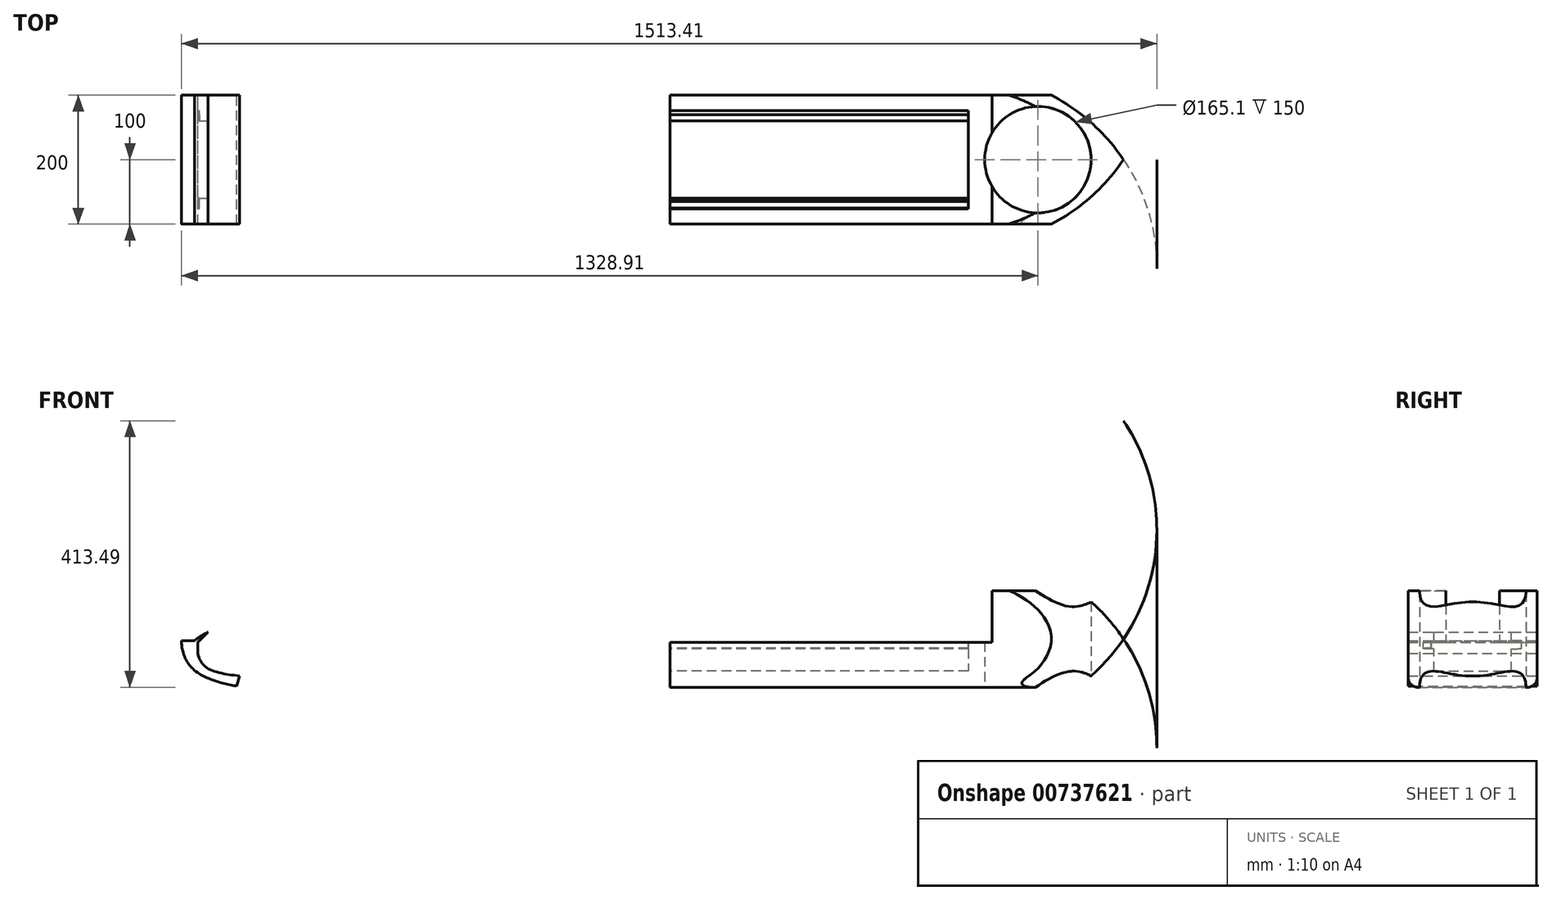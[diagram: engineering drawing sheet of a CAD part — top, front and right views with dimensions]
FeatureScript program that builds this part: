
annotation { "Feature Type Name" : "Feature", "Feature Type Description" : "" }
export const myFeature = defineFeature(function(context is Context, id is Id, definition is map)
    precondition{}
    {
        {
            var Q0;
            Q0=qCreatedBy(makeId("Front.planeOp"),FACE);
            var sketch = newSketch(context, id + "F0", { "sketchPlane" : qUnion([Q0])});
            skLineSegment(sketch, "E0", {"start": v(-811.66, 0) * mm, "end": v(235.58, 0) * mm});
            skPoint(sketch, "E1.visualSharp", {"position": v(572.1, 0) * mm});
            skArc(sketch, "E2", {"start": v(-800.68, 138.75) * mm, "mid": v(-782.15, 142.68) * mm, "end": v(-763.5, 145.97) * mm});
            skArc(sketch, "E3", {"start": v(-763.5, 145.97) * mm, "mid": v(-264.12, 186.3) * mm, "end": v(235.58, 150) * mm});
            skLineSegment(sketch, "E4", {"start": v(235.58, 150) * mm, "end": v(235.58, 0) * mm});
            skLineSegment(sketch, "E5", {"start": v(0, 0) * mm, "end": v(306.95, 0) * mm});
            skPoint(sketch, "E6.orphan", {"position": v(-1022, 0) * mm});
            skLineSegment(sketch, "E7", {"start": v(-918.7, 0) * mm, "end": v(-918.7, 40) * mm});
            skLineSegment(sketch, "E8", {"start": v(-264.12, 186.3) * mm, "end": v(-264.12, 0) * mm});
            skPoint(sketch, "E8.endSnap0", {"position": v(-288.04, 0) * mm});
            skLineSegment(sketch, "E9", {"start": v(-1074.98, 0) * mm, "end": v(-1074.98, 186.3) * mm});
            skLineSegment(sketch, "E10", {"start": v(-1074.98, 186.3) * mm, "end": v(-1074.98, 161.3) * mm});
            skLineSegment(sketch, "E11", {"start": v(-997, 0) * mm, "end": v(-997, 70) * mm});
            skLineSegment(sketch, "E12", {"start": v(-997, 70) * mm, "end": v(235.58, 70) * mm});
            skFitSpline(sketch, "E13", {"points": [v(-1001.83, 72.5) * mm, v(-931.39, 96.18) * mm, v(-756.37, 114.5) * mm, v(-264.12, 141) * mm, v(235.58, 119.1) * mm, v(272.81, 113.33) * mm], "startDerivative": vector(592.82, 474.11) * mm, "endDerivative": vector(301.15, -59.77) * mm});
            skLineSegment(sketch, "E14", {"start": v(-264.12, 70) * mm, "end": v(-264.12, 141) * mm});
            skCircle(sketch, "E15", {"center": v(-946.75, 72.5) * mm, "radius": 2.5 * mm});
            skLineSegment(sketch, "E16.bottom", {"start": v(-862, 70) * mm, "end": v(-851, 70) * mm});
            skLineSegment(sketch, "E16.top", {"start": v(-862, 81) * mm, "end": v(-851, 81) * mm});
            skLineSegment(sketch, "E16.left", {"start": v(-862, 70) * mm, "end": v(-862, 81) * mm});
            skLineSegment(sketch, "E16.right", {"start": v(-851, 70) * mm, "end": v(-851, 81) * mm});
            skLineSegment(sketch, "E17.bottom", {"start": v(-748, 70) * mm, "end": v(-741, 70) * mm});
            skLineSegment(sketch, "E17.top", {"start": v(-748, 77) * mm, "end": v(-741, 77) * mm});
            skLineSegment(sketch, "E17.left", {"start": v(-748, 70) * mm, "end": v(-748, 77) * mm});
            skLineSegment(sketch, "E17.right", {"start": v(-741, 70) * mm, "end": v(-741, 77) * mm});
            skCircle(sketch, "E18", {"center": v(-32.75, 73.75) * mm, "radius": 2.5 * mm});
            skLineSegment(sketch, "E19.bottom", {"start": v(0, 70) * mm, "end": v(7, 70) * mm});
            skLineSegment(sketch, "E19.top", {"start": v(0, 77) * mm, "end": v(7, 77) * mm});
            skLineSegment(sketch, "E19.left", {"start": v(0, 70) * mm, "end": v(0, 77) * mm});
            skLineSegment(sketch, "E19.right", {"start": v(7, 70) * mm, "end": v(7, 77) * mm});
            skLineSegment(sketch, "E20.bottom", {"start": v(136, 70) * mm, "end": v(143, 70) * mm});
            skLineSegment(sketch, "E20.top", {"start": v(136, 77) * mm, "end": v(143, 77) * mm});
            skLineSegment(sketch, "E20.left", {"start": v(136, 70) * mm, "end": v(136, 77) * mm});
            skLineSegment(sketch, "E20.right", {"start": v(143, 70) * mm, "end": v(143, 77) * mm});
            skLineSegment(sketch, "E21", {"start": v(-1001.83, 72.5) * mm, "end": v(-997, 70) * mm});
            skFitSpline(sketch, "E22", {"points": [v(-800.68, 138.75) * mm, v(-939.96, 114.34) * mm, v(-993, 98.83) * mm, v(-1017.8, 82.36) * mm, v(-1021.91, 72.5) * mm, v(-1001.83, 26.4) * mm, v(-918.7, 0) * mm], "startDerivative": vector(-432.5, -65.01) * mm, "endDerivative": vector(192.07, 0) * mm});
            skLineSegment(sketch, "E23", {"start": v(-918.7, 0) * mm, "end": v(-811.66, 0) * mm});
            skLineSegment(sketch, "E24", {"start": v(-997, 70) * mm, "end": v(-980.83, 85.6) * mm});
            skLineSegment(sketch, "E25.bottom", {"start": v(-423, 70) * mm, "end": v(-471, 70) * mm});
            skLineSegment(sketch, "E25.top", {"start": v(-423, 97.8) * mm, "end": v(-471, 97.8) * mm});
            skLineSegment(sketch, "E25.left", {"start": v(-423, 70) * mm, "end": v(-423, 97.8) * mm});
            skLineSegment(sketch, "E25.right", {"start": v(-471, 70) * mm, "end": v(-471, 97.8) * mm});
            skArc(sketch, "E26", {"start": v(-423, 97.8) * mm, "mid": v(-447, 121.8) * mm, "end": v(-471, 97.8) * mm});
            skLineSegment(sketch, "E27", {"start": v(-1001.83, 72.5) * mm, "end": v(-997, 72.5) * mm});
            skLineSegment(sketch, "E28", {"start": v(-980.83, 85.6) * mm, "end": v(-997, 72.5) * mm});
            skLineSegment(sketch, "E29", {"start": v(-997, 70) * mm, "end": v(-997, 72.5) * mm});
            skLineSegment(sketch, "E30", {"start": v(-997, 72.5) * mm, "end": v(-997.16, 76.05) * mm});
            skLineSegment(sketch, "E31", {"start": v(-936.1, 1.72) * mm, "end": v(-932.14, 17.49) * mm});
            skFitSpline(sketch, "E32", {"points": [v(-932.14, 17.49) * mm, v(-987.1, 33.77) * mm, v(-1001.83, 72.5) * mm], "startDerivative": vector(-120.14, 15.95) * mm, "endDerivative": vector(-24.35, 96.08) * mm});
            skLineSegment(sketch, "E33", {"start": v(-1001.83, 72.5) * mm, "end": v(-1021.91, 72.5) * mm});
            skSolve(sketch);
        }
        {
            var Q0;
            {var subQ0=sQuery(id+"F0.wireOp",EDGE,"E9");var subQ1=sQuery(id+"F0.wireOp",EDGE,"ae0f4dbe-3dcb-452f-a479-656d4edaf589");var subQ2=makeQuery(id+"F0.imprint","INTERSECT",VERTEX,{"disambiguationData":[OD(0.0)],"derivedFrom":[subQ1,subQ0]});Q0=makeQuery(id+"F0.imprint","IMPRINT",FACE,{"disambiguationData":[TD([[makeQuery(id+"F0.imprint","IMPRINT",EDGE,{"disambiguationData":[TD([[subQ2,1.0]])],"derivedFrom":subQ1}),1.0]])]});}
            var Q1;
            {var subQ0=sQuery(id+"F0.wireOp",EDGE,"E5");var subQ1=sQuery(id+"F0.wireOp",EDGE,"E0");var subQ2=makeQuery(id+"F0.imprint","INTERSECT",VERTEX,{"derivedFrom":[subQ1,subQ0]});Q1=makeQuery(id+"F0.imprint","IMPRINT",FACE,{"disambiguationData":[TD([[makeQuery(id+"F0.imprint","IMPRINT",EDGE,{"disambiguationData":[TD([[subQ2,1.0]])],"derivedFrom":subQ1}),1.0]])]});}
            var Q2;
            {var subQ0=sQuery(id+"F0.wireOp",EDGE,"fSm7vGDM-Fk6q-mBao-oBgU-qa2BAWfb7Zod");Q2=makeQuery(id+"F0.imprint","IMPRINT",FACE,{"disambiguationData":[TD([[makeQuery(id+"F0.imprint","IMPRINT",EDGE,{"derivedFrom":subQ0}),1.0]])]});}
            var Q3;
            {var subQ3=sQuery(id+"F0.wireOp",EDGE,"ae0f4dbe-3dcb-452f-a479-656d4edaf589");var subQ5=sQuery(id+"F0.wireOp",EDGE,"E0");var subQ6=makeQuery(id+"F0.imprint","INTERSECT",VERTEX,{"derivedFrom":[subQ5,subQ3]});Q3=makeQuery(id+"F0.imprint","IMPRINT",FACE,{"disambiguationData":[TD([[makeQuery(id+"F0.imprint","IMPRINT",EDGE,{"disambiguationData":[TD([[subQ6,-1.0]])],"derivedFrom":subQ5}),1.0]])]});}
            var Q4;
            {var subQ0=sQuery(id+"F0.wireOp",EDGE,"E8");var subQ1=sQuery(id+"F0.wireOp",EDGE,"E3");var subQ2=makeQuery(id+"F0.imprint","INTERSECT",VERTEX,{"derivedFrom":[subQ1,subQ0]});Q4=makeQuery(id+"F0.imprint","IMPRINT",FACE,{"disambiguationData":[TD([[makeQuery(id+"F0.imprint","IMPRINT",EDGE,{"disambiguationData":[TD([[subQ2,1.0]])],"derivedFrom":subQ1}),-1.0]])]});}
            var Q5;
            {var subQ0=sQuery(id+"F0.wireOp",EDGE,"E8");var subQ1=sQuery(id+"F0.wireOp",EDGE,"E3");var subQ2=makeQuery(id+"F0.imprint","INTERSECT",VERTEX,{"derivedFrom":[subQ1,subQ0]});Q5=makeQuery(id+"F0.imprint","IMPRINT",FACE,{"disambiguationData":[TD([[makeQuery(id+"F0.imprint","IMPRINT",EDGE,{"disambiguationData":[TD([[subQ2,-1.0]])],"derivedFrom":subQ1}),-1.0]])]});}
            var Q6;
            {var subQ6=sQuery(id+"F0.wireOp",EDGE,"fSm7vGDM-Fk6q-mBao-oBgU-qa2BAWfb7Zod");Q6=makeQuery(id+"F0.imprint","IMPRINT",FACE,{"disambiguationData":[TD([[makeQuery(id+"F0.imprint","IMPRINT",EDGE,{"derivedFrom":subQ6}),-1.0]])]});}
            var Q7;
            {var subQ0=sQuery(id+"F0.wireOp",EDGE,"mQbvmNGf-kzkf-nsPK-earb-okNbtzBX8b3B");Q7=makeQuery(id+"F0.imprint","IMPRINT",FACE,{"disambiguationData":[TD([[makeQuery(id+"F0.imprint","IMPRINT",EDGE,{"derivedFrom":subQ0}),1.0]])]});}
            var Q8;
            {var subQ4=sQuery(id+"F0.wireOp",EDGE,"E2");Q8=makeQuery(id+"F0.imprint","IMPRINT",FACE,{"disambiguationData":[TD([[makeQuery(id+"F0.imprint","IMPRINT",EDGE,{"derivedFrom":subQ4}),-1.0]])]});}
            var Q9;
            {var subQ5=sQuery(id+"F0.wireOp",EDGE,"hbAUqSZh-UFjw-PT6U-r02d-sjCPNXMwl6o5");Q9=makeQuery(id+"F0.imprint","IMPRINT",FACE,{"disambiguationData":[TD([[makeQuery(id+"F0.imprint","IMPRINT",EDGE,{"derivedFrom":subQ5}),-1.0]])]});}
            var Q10;
            {var subQ3=sQuery(id+"F0.wireOp",EDGE,"E14");Q10=makeQuery(id+"F0.imprint","IMPRINT",FACE,{"disambiguationData":[TD([[makeQuery(id+"F0.imprint","IMPRINT",EDGE,{"derivedFrom":subQ3}),1.0]])]});}
            var Q11;
            {var subQ5=sQuery(id+"F0.wireOp",EDGE,"E14");Q11=makeQuery(id+"F0.imprint","IMPRINT",FACE,{"disambiguationData":[TD([[makeQuery(id+"F0.imprint","IMPRINT",EDGE,{"derivedFrom":subQ5}),-1.0]])]});}
            var Q12;
            {var subQ1=sQuery(id+"F0.wireOp",EDGE,"E3");var subQ7=sQuery(id+"F0.wireOp",EDGE,"E4");var subQ8=makeQuery(id+"F0.imprint","INTERSECT",VERTEX,{"derivedFrom":[subQ1,subQ7]});Q12=makeQuery(id+"F0.imprint","IMPRINT",FACE,{"disambiguationData":[TD([[makeQuery(id+"F0.imprint","IMPRINT",EDGE,{"disambiguationData":[TD([[subQ8,1.0]])],"derivedFrom":subQ1}),-1.0]])]});}
            var Q13;
            {var subQ0=sQuery(id+"F0.wireOp",EDGE,"JpqKEAA7-A54T-XD6g-pLle-evRgGPghxYK8");Q13=makeQuery(id+"F0.imprint","IMPRINT",FACE,{"disambiguationData":[TD([[makeQuery(id+"F0.imprint","IMPRINT",EDGE,{"derivedFrom":subQ0}),1.0]])]});}
            var Q14;
            Q14=makeQuery(id+"F0.imprint","IMPRINT",FACE,{"disambiguationData":[TD([[makeQuery(id+"F0.imprint","IMPRINT",EDGE,{"derivedFrom":sQuery(id+"F0.wireOp",EDGE,"E15")}),1.0]])]});
            var Q15;
            Q15=makeQuery(id+"F0.imprint","IMPRINT",FACE,{"disambiguationData":[TD([[makeQuery(id+"F0.imprint","IMPRINT",EDGE,{"derivedFrom":sQuery(id+"F0.wireOp",EDGE,"E16.bottom")}),1.0]])]});
            var Q16;
            Q16=makeQuery(id+"F0.imprint","IMPRINT",FACE,{"disambiguationData":[TD([[makeQuery(id+"F0.imprint","IMPRINT",EDGE,{"derivedFrom":sQuery(id+"F0.wireOp",EDGE,"E17.bottom")}),1.0]])]});
            var Q17;
            {var subQ11=sQuery(id+"F0.wireOp",EDGE,"LO9gbCX8-fOce-iITb-FMT8-DmU32IrCbeHD");Q17=makeQuery(id+"F0.imprint","IMPRINT",FACE,{"disambiguationData":[TD([[makeQuery(id+"F0.imprint","IMPRINT",EDGE,{"derivedFrom":subQ11}),1.0]])]});}
            var Q18;
            {var subQ0=sQuery(id+"F0.wireOp",EDGE,"LO9gbCX8-fOce-iITb-FMT8-DmU32IrCbeHD");Q18=makeQuery(id+"F0.imprint","IMPRINT",FACE,{"disambiguationData":[TD([[makeQuery(id+"F0.imprint","IMPRINT",EDGE,{"derivedFrom":subQ0}),-1.0]])]});}
            var Q19;
            {var subQ4=sQuery(id+"F0.wireOp",EDGE,"E16.bottom");Q19=makeQuery(id+"F0.imprint","IMPRINT",FACE,{"disambiguationData":[TD([[makeQuery(id+"F0.imprint","IMPRINT",EDGE,{"derivedFrom":subQ4}),-1.0]])]});}
            var Q20;
            {var subQ0=sQuery(id+"F0.wireOp",EDGE,"E21");Q20=makeQuery(id+"F0.imprint","IMPRINT",FACE,{"disambiguationData":[TD([[makeQuery(id+"F0.imprint","IMPRINT",EDGE,{"derivedFrom":subQ0}),1.0]])]});}
            var Q21;
            {var subQ0=sQuery(id+"F0.wireOp",EDGE,"22GWFGu7-XqVd-ZN1t-vtD5-4GBQYmcN7Nnm");Q21=makeQuery(id+"F0.imprint","IMPRINT",FACE,{"disambiguationData":[TD([[makeQuery(id+"F0.imprint","IMPRINT",EDGE,{"derivedFrom":subQ0}),1.0]])]});}
            var Q22;
            {var subQ0=sQuery(id+"F0.wireOp",EDGE,"E28");Q22=makeQuery(id+"F0.imprint","IMPRINT",FACE,{"disambiguationData":[TD([[makeQuery(id+"F0.imprint","IMPRINT",EDGE,{"derivedFrom":subQ0}),-1.0]])]});}
            var Q23;
            Q23=makeQuery(id+"F0.imprint","IMPRINT",FACE,{"disambiguationData":[TD([[makeQuery(id+"F0.imprint","IMPRINT",EDGE,{"derivedFrom":sQuery(id+"F0.wireOp",EDGE,"E24")}),1.0]])]});
            var Q24;
            {var subQ0=sQuery(id+"F0.wireOp",EDGE,"E27");Q24=makeQuery(id+"F0.imprint","IMPRINT",FACE,{"disambiguationData":[TD([[makeQuery(id+"F0.imprint","IMPRINT",EDGE,{"derivedFrom":subQ0}),1.0]])]});}
            var Q25;
            {var subQ5=sQuery(id+"F0.wireOp",EDGE,"E33");Q25=makeQuery(id+"F0.imprint","IMPRINT",FACE,{"disambiguationData":[TD([[makeQuery(id+"F0.imprint","IMPRINT",EDGE,{"derivedFrom":subQ5}),1.0]])]});}
            var Q26;
            {var subQ0=sQuery(id+"F0.wireOp",EDGE,"E21");Q26=makeQuery(id+"F0.imprint","IMPRINT",FACE,{"disambiguationData":[TD([[makeQuery(id+"F0.imprint","IMPRINT",EDGE,{"derivedFrom":subQ0}),-1.0]])]});}
            var Q27;
            {var subQ5=sQuery(id+"F0.wireOp",EDGE,"E31");Q27=makeQuery(id+"F0.imprint","IMPRINT",FACE,{"disambiguationData":[TD([[makeQuery(id+"F0.imprint","IMPRINT",EDGE,{"derivedFrom":subQ5}),1.0]])]});}
            extrude(context, id + "F1", {"entities" : qUnion([Q0, Q1, Q2, Q3, Q4, Q5, Q6, Q7, Q8, Q9, Q10, Q11, Q12, Q13, Q14, Q15, Q16, Q17, Q18, Q19, Q20, Q21, Q22, Q23, Q24, Q25, Q26, Q27]), "depth" : 200 * mm, "offsetDistance" : 25 * mm});
        }
        {
            var Q0;
            Q0=makeQuery(id+"F1.opExtrude","CAP_FACE",FACE,{"disambiguationData":[OSD([sQuery(id+"F0.wireOp",EDGE,"E0"),sQuery(id+"F0.wireOp",EDGE,"cFxAAAna-ocuM-yQAM-ZuZ0-mVdnYAltbvAJ"),sQuery(id+"F0.wireOp",EDGE,"E1.filletArc"),sQuery(id+"F0.wireOp",EDGE,"dOAzaddM-v2gw-8Rk0-Et5F-y7kRLDfQY5BQ"),sQuery(id+"F0.wireOp",EDGE,"E2"),sQuery(id+"F0.wireOp",EDGE,"1fbf2cc0-c2b9-49e0-98a3-bc7080fc43d8"),sQuery(id+"F0.wireOp",EDGE,"E3")])],"isStart":false});
            var sketch = newSketch(context, id + "F2", { "sketchPlane" : qUnion([Q0])});
            skSolve(sketch);
        }
        {
            var Q0;
            Q0=qCreatedBy(makeId("Front.planeOp"),FACE);
            cPlane(context, id + "F3", {"entities" : qUnion([Q0]), "cplaneType" : CPlaneType.OFFSET, "offset" : 100 * mm, "width" : 150 * mm, "height" : 150 * mm});
        }
        {
            var Q0;
            Q0=qCreatedBy(makeId("Right.planeOp"),FACE);
            var sketch = newSketch(context, id + "F4", { "sketchPlane" : qUnion([Q0])});
            skLineSegment(sketch, "E34.0", {"start": v(0, 145.97) * mm, "end": v(0, 186.32) * mm});
            skLineSegment(sketch, "E35.0", {"start": v(-200, 145.97) * mm, "end": v(-200, 186.32) * mm});
            skLineSegment(sketch, "E36", {"start": v(135.3, 186.32) * mm, "end": v(135.3, -46.02) * mm});
            skLineSegment(sketch, "E37", {"start": v(135.3, -46.02) * mm, "end": v(0, -46.02) * mm});
            skLineSegment(sketch, "E38", {"start": v(0, -46.02) * mm, "end": v(0, 145.97) * mm});
            skLineSegment(sketch, "E39", {"start": v(-200, 186.32) * mm, "end": v(-200, -70.3) * mm});
            skLineSegment(sketch, "E40.0.0", {"start": v(-155.46, 145.97) * mm, "end": v(-200, 145.97) * mm});
            skFitSpline(sketch, "E40.0.1", {"points": [v(-155.46, 150) * mm, v(-153.49, 150.19) * mm, v(-149.43, 150.54) * mm, v(-144.12, 150.92) * mm, v(-139.72, 151.2) * mm, v(-136.35, 151.38) * mm, v(-132.9, 151.55) * mm, v(-129.96, 151.68) * mm, v(-127.58, 151.77) * mm, v(-125.18, 151.86) * mm, v(-122.18, 151.95) * mm, v(-118.55, 152.05) * mm, v(-114.9, 152.13) * mm, v(-111.21, 152.2) * mm, v(-107.5, 152.24) * mm, v(-103.78, 152.26) * mm, v(-100.65, 152.27) * mm, v(-98.13, 152.27) * mm, v(-95.63, 152.26) * mm, v(-92.51, 152.24) * mm, v(-88.8, 152.2) * mm, v(-85.12, 152.13) * mm, v(-81.47, 152.05) * mm, v(-77.84, 151.95) * mm, v(-74.24, 151.84) * mm, v(-71.26, 151.72) * mm, v(-68.9, 151.63) * mm, v(-66.55, 151.52) * mm, v(-63.67, 151.38) * mm, v(-60.3, 151.2) * mm, v(-55.89, 150.92) * mm, v(-50.57, 150.54) * mm, v(-46.51, 150.19) * mm, v(-44.54, 150) * mm]});
            skLineSegment(sketch, "E40.0.2", {"start": v(0, 145.97) * mm, "end": v(-44.54, 145.97) * mm});
            skLineSegment(sketch, "E40.0.3", {"start": v(0, 186.32) * mm, "end": v(0, 145.97) * mm});
            skLineSegment(sketch, "E40.0.4", {"start": v(0, 145.97) * mm, "end": v(-200, 145.97) * mm});
            skFitSpline(sketch, "E41.0.1", {"points": [v(-155.46, 150) * mm, v(-153.49, 150.19) * mm, v(-149.43, 150.54) * mm, v(-144.12, 150.92) * mm, v(-139.72, 151.2) * mm, v(-136.35, 151.38) * mm, v(-132.9, 151.55) * mm, v(-129.96, 151.68) * mm, v(-127.58, 151.77) * mm, v(-125.18, 151.86) * mm, v(-122.18, 151.95) * mm, v(-118.55, 152.05) * mm, v(-114.9, 152.13) * mm, v(-111.21, 152.2) * mm, v(-107.5, 152.24) * mm, v(-103.78, 152.26) * mm, v(-100.65, 152.27) * mm, v(-98.13, 152.27) * mm, v(-95.63, 152.26) * mm, v(-92.51, 152.24) * mm, v(-88.8, 152.2) * mm, v(-85.12, 152.13) * mm, v(-81.47, 152.05) * mm, v(-77.84, 151.95) * mm, v(-74.24, 151.84) * mm, v(-71.26, 151.72) * mm, v(-68.9, 151.63) * mm, v(-66.55, 151.52) * mm, v(-63.67, 151.38) * mm, v(-60.3, 151.2) * mm, v(-55.89, 150.92) * mm, v(-50.57, 150.54) * mm, v(-46.51, 150.19) * mm, v(-44.54, 150) * mm]});
            skLineSegment(sketch, "E42", {"start": v(0, 186.32) * mm, "end": v(-200, 186.32) * mm});
            skLineSegment(sketch, "E43", {"start": v(0, -46.02) * mm, "end": v(-200, -46.02) * mm});
            skLineSegment(sketch, "E44", {"start": v(-200, -46.02) * mm, "end": v(-305.06, -46.02) * mm});
            skLineSegment(sketch, "E45", {"start": v(-305.06, -46.02) * mm, "end": v(-305.06, 186.32) * mm});
            skLineSegment(sketch, "E46", {"start": v(135.3, 186.32) * mm, "end": v(135.3, 224.68) * mm});
            skLineSegment(sketch, "E47", {"start": v(135.3, 224.68) * mm, "end": v(-305.06, 224.68) * mm});
            skLineSegment(sketch, "E48", {"start": v(0, 186.32) * mm, "end": v(135.3, 186.32) * mm});
            skLineSegment(sketch, "E49", {"start": v(-200, 186.32) * mm, "end": v(-305.06, 186.32) * mm});
            skLineSegment(sketch, "E50", {"start": v(-305.06, 224.68) * mm, "end": v(-305.06, 186.32) * mm});
            skLineSegment(sketch, "E51.0", {"start": v(0, 0) * mm, "end": v(-200, 0) * mm});
            skSolve(sketch);
        }
        {
            var Q0;
            Q0=qCreatedBy(id+"F3.planeOp",FACE);
            var sketch = newSketch(context, id + "F5", { "sketchPlane" : qUnion([Q0])});
            skLineSegment(sketch, "E52.0", {"start": v(235.58, 150) * mm, "end": v(235.58, 150) * mm});
            skLineSegment(sketch, "E53", {"start": v(235.58, 75) * mm, "end": v(439.83, 75) * mm});
            skLineSegment(sketch, "E54", {"start": v(235.58, 75) * mm, "end": v(235.58, 205.26) * mm});
            skArc(sketch, "E55", {"start": v(439.83, 75) * mm, "mid": v(351.28, 161.42) * mm, "end": v(235.58, 205.26) * mm});
            skSolve(sketch);
        }
        {
            var Q0;
            Q0=makeQuery(id+"F5.imprint","IMPRINT",FACE,{"disambiguationData":[TD([[makeQuery(id+"F5.imprint","IMPRINT",EDGE,{"derivedFrom":sQuery(id+"F5.wireOp",EDGE,"E53")}),1.0]])]});
            var Q1;
            Q1=sQuery(id+"F5.wireOp",EDGE,"E53");
            revolve(context, id + "F6", {"operationType" : NewBodyOperationType.ADD, "surfaceOperationType" : NewSurfaceOperationType.NEW, "entities" : qUnion([Q0]), "axis" : qUnion([Q1]), "revolveType" : RevolveType.FULL});
        }
        {
            var Q0;
            Q0=qCreatedBy(makeId("Top.planeOp"),FACE);
            var sketch = newSketch(context, id + "F7", { "sketchPlane" : qUnion([Q0])});
            skLineSegment(sketch, "E56.0", {"start": v(235.58, -230.26) * mm, "end": v(235.58, 30.26) * mm});
            skLineSegment(sketch, "E57", {"start": v(235.58, -100) * mm, "end": v(549.76, -100) * mm});
            skCircle(sketch, "E58", {"center": v(306.95, -100) * mm, "radius": 82.55 * mm});
            skSolve(sketch);
        }
        {
            var Q0;
            Q0=makeQuery(id+"F4.imprint","IMPRINT",FACE,{"disambiguationData":[TD([[makeQuery(id+"F4.imprint","IMPRINT",EDGE,{"derivedFrom":sQuery(id+"F4.wireOp",EDGE,"E36")}),-1.0]])]});
            var Q1;
            {var subQ0=sQuery(id+"F4.wireOp",EDGE,"E35.0");Q1=makeQuery(id+"F4.imprint","IMPRINT",FACE,{"disambiguationData":[TD([[makeQuery(id+"F4.imprint","IMPRINT",EDGE,{"derivedFrom":subQ0}),1.0]])]});}
            var Q2;
            Q2=makeQuery(id+"F4.imprint","IMPRINT",FACE,{"disambiguationData":[TD([[makeQuery(id+"F4.imprint","IMPRINT",EDGE,{"derivedFrom":sQuery(id+"F4.wireOp",EDGE,"E42")}),-1.0]])]});
            var Q3;
            {var subQ0=sQuery(id+"F4.wireOp",EDGE,"E43");Q3=makeQuery(id+"F4.imprint","IMPRINT",FACE,{"disambiguationData":[TD([[makeQuery(id+"F4.imprint","IMPRINT",EDGE,{"derivedFrom":subQ0}),-1.0]])]});}
            extrude(context, id + "F8", {"entities" : qUnion([Q0, Q1, Q2, Q3]), "operationType" : NewBodyOperationType.REMOVE, "endBound" : BoundingType.THROUGH_ALL, "depth" : 25 * mm, "offsetDistance" : 25 * mm});
        }
        {
            var Q0;
            Q0=makeQuery(id+"F2.imprint","IMPRINT",FACE,{"disambiguationData":[TD([[makeQuery(id+"F2.imprint","IMPRINT",EDGE,{"derivedFrom":makeQuery(id+"F1.opExtrude","CAP_EDGE",EDGE,{"disambiguationData":[OSD([sQuery(id+"F0.wireOp",EDGE,"E0")])],"isStart":false})}),1.0]])]});
            var sketch = newSketch(context, id + "F9", { "sketchPlane" : qUnion([Q0])});
            skLineSegment(sketch, "E59.0", {"start": v(235.58, 158.48) * mm, "end": v(235.58, 150) * mm});
            skLineSegment(sketch, "E60", {"start": v(235.58, 150) * mm, "end": v(322.77, 150) * mm});
            skLineSegment(sketch, "E61", {"start": v(322.77, 150) * mm, "end": v(322.77, 208) * mm});
            skLineSegment(sketch, "E62", {"start": v(322.77, 208) * mm, "end": v(235.58, 208) * mm});
            skLineSegment(sketch, "E63", {"start": v(235.58, 208) * mm, "end": v(235.58, 150) * mm});
            skLineSegment(sketch, "E64", {"start": v(235.58, 150) * mm, "end": v(235.58, -52.6) * mm});
            skLineSegment(sketch, "E65", {"start": v(235.58, -52.6) * mm, "end": v(259.84, -52.6) * mm});
            skLineSegment(sketch, "E66", {"start": v(259.84, -52.6) * mm, "end": v(259.84, -21.36) * mm});
            skLineSegment(sketch, "E67", {"start": v(259.84, -21.36) * mm, "end": v(235.58, -21.36) * mm});
            skSolve(sketch);
        }
        {
            var Q0;
            {var subQ0=sQuery(id+"F9.wireOp",EDGE,"E60");Q0=makeQuery(id+"F9.imprint","IMPRINT",FACE,{"disambiguationData":[TD([[makeQuery(id+"F9.imprint","IMPRINT",EDGE,{"derivedFrom":subQ0}),1.0]])]});}
            var Q1;
            {var subQ0=sQuery(id+"F9.wireOp",EDGE,"E65");Q1=makeQuery(id+"F9.imprint","IMPRINT",FACE,{"disambiguationData":[TD([[makeQuery(id+"F9.imprint","IMPRINT",EDGE,{"derivedFrom":subQ0}),1.0]])]});}
            extrude(context, id + "F10", {"entities" : qUnion([Q0, Q1]), "operationType" : NewBodyOperationType.REMOVE, "endBound" : BoundingType.THROUGH_ALL, "oppositeDirection" : true, "depth" : 25 * mm, "offsetDistance" : 25 * mm});
        }
        {
            var Q0;
            Q0=qCreatedBy(makeId("Right.planeOp"),FACE);
            cPlane(context, id + "F11", {"entities" : qUnion([Q0]), "cplaneType" : CPlaneType.OFFSET, "offset" : 1022 * mm, "oppositeDirection" : true, "width" : 150 * mm, "height" : 150 * mm});
        }
        {
            var Q0;
            Q0=qCreatedBy(id+"F11.planeOp",FACE);
            var sketch = newSketch(context, id + "F12", { "sketchPlane" : qUnion([Q0])});
            skLineSegment(sketch, "E68.bottom", {"start": v(0, 0) * mm, "end": v(-200, 0) * mm});
            skLineSegment(sketch, "E68.top", {"start": v(0, 186.3) * mm, "end": v(-200, 186.3) * mm});
            skLineSegment(sketch, "E68.left", {"start": v(0, 0) * mm, "end": v(0, 186.3) * mm});
            skLineSegment(sketch, "E68.right", {"start": v(-200, 0) * mm, "end": v(-200, 186.3) * mm});
            skLineSegment(sketch, "E69", {"start": v(0, 61) * mm, "end": v(-25, 61) * mm});
            skLineSegment(sketch, "E70", {"start": v(-25, 61) * mm, "end": v(-25, 0) * mm});
            skLineSegment(sketch, "E71.bottom", {"start": v(-25, 61) * mm, "end": v(-35, 61) * mm});
            skLineSegment(sketch, "E71.top", {"start": v(-25, 71) * mm, "end": v(-35, 71) * mm});
            skLineSegment(sketch, "E71.left", {"start": v(-25, 61) * mm, "end": v(-25, 71) * mm});
            skLineSegment(sketch, "E71.right", {"start": v(-35, 61) * mm, "end": v(-35, 71) * mm});
            skLineSegment(sketch, "E72", {"start": v(-100, 0) * mm, "end": v(-100, 186.3) * mm});
            skLineSegment(sketch, "E73.MirrorCS", {"start": v(-165, 61) * mm, "end": v(-165, 71) * mm});
            skLineSegment(sketch, "E74.MirrorCS", {"start": v(-175, 71) * mm, "end": v(-165, 71) * mm});
            skLineSegment(sketch, "E75.MirrorCS", {"start": v(-175, 61) * mm, "end": v(-165, 61) * mm});
            skLineSegment(sketch, "E76.MirrorCS", {"start": v(-175, 61) * mm, "end": v(-175, 71) * mm});
            skLineSegment(sketch, "E77.bottom", {"start": v(-23.5, 72.5) * mm, "end": v(-36.5, 72.5) * mm});
            skLineSegment(sketch, "E77.top", {"start": v(-23.5, 59.5) * mm, "end": v(-36.5, 59.5) * mm});
            skLineSegment(sketch, "E77.left", {"start": v(-23.5, 72.5) * mm, "end": v(-23.5, 59.5) * mm});
            skLineSegment(sketch, "E77.right", {"start": v(-36.5, 72.5) * mm, "end": v(-36.5, 59.5) * mm});
            skLineSegment(sketch, "E78", {"start": v(-23.5, 59.5) * mm, "end": v(-23.5, 0) * mm});
            skLineSegment(sketch, "E79", {"start": v(-23.5, 59.5) * mm, "end": v(0, 59.5) * mm});
            skLineSegment(sketch, "E80", {"start": v(-30, 72.5) * mm, "end": v(-30, 161.3) * mm});
            skLineSegment(sketch, "E81", {"start": v(-30, 59.5) * mm, "end": v(-30, 25) * mm});
            skLineSegment(sketch, "E82", {"start": v(-30, 161.3) * mm, "end": v(-100, 161.3) * mm});
            skLineSegment(sketch, "E83", {"start": v(-30, 25) * mm, "end": v(-100, 25) * mm});
            skLineSegment(sketch, "E84.bottom", {"start": v(-24, 72) * mm, "end": v(-36, 72) * mm});
            skLineSegment(sketch, "E84.top", {"start": v(-24, 60) * mm, "end": v(-36, 60) * mm});
            skLineSegment(sketch, "E84.left", {"start": v(-24, 72) * mm, "end": v(-24, 60) * mm});
            skLineSegment(sketch, "E84.right", {"start": v(-36, 72) * mm, "end": v(-36, 60) * mm});
            skLineSegment(sketch, "E85", {"start": v(-24, 60) * mm, "end": v(0, 60) * mm});
            skLineSegment(sketch, "E86", {"start": v(-24, 60) * mm, "end": v(-24, 0) * mm});
            skLineSegment(sketch, "E87", {"start": v(-30, 72.5) * mm, "end": v(-30, 71) * mm});
            skLineSegment(sketch, "E88", {"start": v(-30, 59.5) * mm, "end": v(-30, 60.5) * mm});
            skLineSegment(sketch, "E89.MirrorCS", {"start": v(-176, 60) * mm, "end": v(-164, 60) * mm});
            skLineSegment(sketch, "E90.MirrorCS", {"start": v(-176, 72) * mm, "end": v(-164, 72) * mm});
            skLineSegment(sketch, "E91.MirrorCS", {"start": v(-170, 59.5) * mm, "end": v(-170, 60.5) * mm});
            skLineSegment(sketch, "E92.MirrorCS", {"start": v(-176.5, 59.5) * mm, "end": v(-163.5, 59.5) * mm});
            skLineSegment(sketch, "E93.MirrorCS", {"start": v(-170, 72.5) * mm, "end": v(-170, 71) * mm});
            skLineSegment(sketch, "E94.MirrorCS", {"start": v(-176.5, 72.5) * mm, "end": v(-163.5, 72.5) * mm});
            skLineSegment(sketch, "E95.MirrorCS", {"start": v(-164, 72) * mm, "end": v(-164, 60) * mm});
            skLineSegment(sketch, "E96.MirrorCS", {"start": v(-176, 72) * mm, "end": v(-176, 60) * mm});
            skLineSegment(sketch, "E97.MirrorCS", {"start": v(-163.5, 72.5) * mm, "end": v(-163.5, 59.5) * mm});
            skLineSegment(sketch, "E98.MirrorCS", {"start": v(-176.5, 72.5) * mm, "end": v(-176.5, 59.5) * mm});
            skLineSegment(sketch, "E99.MirrorCS", {"start": v(-170, 59.5) * mm, "end": v(-170, 25) * mm});
            skLineSegment(sketch, "E100.MirrorCS", {"start": v(-170, 25) * mm, "end": v(-100, 25) * mm});
            skLineSegment(sketch, "E101.MirrorCS", {"start": v(-170, 161.3) * mm, "end": v(-100, 161.3) * mm});
            skLineSegment(sketch, "E102.MirrorCS", {"start": v(-170, 72.5) * mm, "end": v(-170, 161.3) * mm});
            skLineSegment(sketch, "E103", {"start": v(-23.5, 61) * mm, "end": v(-24, 61) * mm});
            skLineSegment(sketch, "E104", {"start": v(-23.5, 61) * mm, "end": v(-23.5, 60) * mm});
            skLineSegment(sketch, "E105", {"start": v(-24, 60) * mm, "end": v(-24, 59.5) * mm});
            skLineSegment(sketch, "E106", {"start": v(-25, 59.5) * mm, "end": v(-25, 60) * mm});
            skLineSegment(sketch, "E107.MirrorCS", {"start": v(-176.5, 61) * mm, "end": v(-176, 61) * mm});
            skLineSegment(sketch, "E108.MirrorCS", {"start": v(-176.5, 61) * mm, "end": v(-176.5, 60) * mm});
            skLineSegment(sketch, "E109.MirrorCS", {"start": v(-175, 59.5) * mm, "end": v(-175, 60) * mm});
            skLineSegment(sketch, "E110.MirrorCS", {"start": v(-176, 60) * mm, "end": v(-176, 59.5) * mm});
            skLineSegment(sketch, "E111", {"start": v(-175, 61) * mm, "end": v(-175, 60) * mm});
            skLineSegment(sketch, "E112", {"start": v(-175, 61) * mm, "end": v(-176, 61) * mm});
            skLineSegment(sketch, "E113", {"start": v(-176, 60) * mm, "end": v(-176.5, 60) * mm});
            skLineSegment(sketch, "E114", {"start": v(-30, 72) * mm, "end": v(-30, 72.5) * mm});
            skLineSegment(sketch, "E115", {"start": v(-170, 59.5) * mm, "end": v(-170, 60) * mm});
            skPoint(sketch, "E116", {"position": v(-30.15, 60.5) * mm});
            skLineSegment(sketch, "E117", {"start": v(-30, 60.5) * mm, "end": v(-30, 61) * mm});
            skLineSegment(sketch, "E118", {"start": v(-170, 60.5) * mm, "end": v(-170, 61) * mm});
            skLineSegment(sketch, "E119", {"start": v(-36.5, 72.5) * mm, "end": v(-40, 72.5) * mm});
            skLineSegment(sketch, "E120", {"start": v(-40, 72.5) * mm, "end": v(-40, 161.3) * mm});
            skLineSegment(sketch, "E121", {"start": v(-36.5, 59.5) * mm, "end": v(-40, 59.5) * mm});
            skLineSegment(sketch, "E122", {"start": v(-40, 59.5) * mm, "end": v(-40, 0) * mm});
            skLineSegment(sketch, "E123", {"start": v(-40, 72.5) * mm, "end": v(-40, 59.5) * mm});
            skLineSegment(sketch, "E124.MirrorCS", {"start": v(-160, 72.5) * mm, "end": v(-160, 161.3) * mm});
            skLineSegment(sketch, "E125.MirrorCS", {"start": v(-160, 72.5) * mm, "end": v(-160, 59.5) * mm});
            skLineSegment(sketch, "E126.MirrorCS", {"start": v(-160, 59.5) * mm, "end": v(-160, 0) * mm});
            skLineSegment(sketch, "E127.MirrorCS", {"start": v(-163.5, 59.5) * mm, "end": v(-160, 59.5) * mm});
            skLineSegment(sketch, "E128.MirrorCS", {"start": v(-163.5, 72.5) * mm, "end": v(-160, 72.5) * mm});
            skSolve(sketch);
        }
        {
            var Q0;
            {var subQ8=sQuery(id+"F12.wireOp",EDGE,"E76.MirrorCS");Q0=makeQuery(id+"F12.imprint","IMPRINT",FACE,{"disambiguationData":[TD([[makeQuery(id+"F12.imprint","IMPRINT",EDGE,{"derivedFrom":subQ8}),1.0]])]});}
            var Q1;
            {var subQ3=sQuery(id+"F12.wireOp",EDGE,"E71.left");Q1=makeQuery(id+"F12.imprint","IMPRINT",FACE,{"disambiguationData":[TD([[makeQuery(id+"F12.imprint","IMPRINT",EDGE,{"derivedFrom":subQ3}),1.0]])]});}
            var Q2;
            {var subQ4=sQuery(id+"F12.wireOp",EDGE,"E71.left");Q2=makeQuery(id+"F12.imprint","IMPRINT",FACE,{"disambiguationData":[TD([[makeQuery(id+"F12.imprint","IMPRINT",EDGE,{"derivedFrom":subQ4}),-1.0]])]});}
            var Q3;
            {var subQ1=sQuery(id+"F12.wireOp",EDGE,"E69");var subQ3=sQuery(id+"F12.wireOp",EDGE,"E84.left");var subQ4=makeQuery(id+"F12.imprint","INTERSECT",VERTEX,{"derivedFrom":[subQ1,subQ3,sQuery(id+"F12.wireOp",EDGE,"E103")]});Q3=makeQuery(id+"F12.imprint","IMPRINT",FACE,{"disambiguationData":[TD([[makeQuery(id+"F12.imprint","IMPRINT",EDGE,{"disambiguationData":[TD([[subQ4,-1.0]])],"derivedFrom":subQ1}),1.0]])]});}
            var Q4;
            {var subQ0=sQuery(id+"F12.wireOp",EDGE,"E73.MirrorCS");Q4=makeQuery(id+"F12.imprint","IMPRINT",FACE,{"disambiguationData":[TD([[makeQuery(id+"F12.imprint","IMPRINT",EDGE,{"derivedFrom":subQ0}),1.0]])]});}
            var Q5;
            {var subQ6=sQuery(id+"F12.wireOp",EDGE,"E97.MirrorCS");Q5=makeQuery(id+"F12.imprint","IMPRINT",FACE,{"disambiguationData":[TD([[makeQuery(id+"F12.imprint","IMPRINT",EDGE,{"derivedFrom":subQ6}),-1.0]])]});}
            var Q6;
            {var subQ10=sQuery(id+"F12.wireOp",EDGE,"E91.MirrorCS");Q6=makeQuery(id+"F12.imprint","IMPRINT",FACE,{"disambiguationData":[TD([[makeQuery(id+"F12.imprint","IMPRINT",EDGE,{"derivedFrom":subQ10}),-1.0]])]});}
            var Q7;
            {var subQ3=sQuery(id+"F12.wireOp",EDGE,"E111");Q7=makeQuery(id+"F12.imprint","IMPRINT",FACE,{"disambiguationData":[TD([[makeQuery(id+"F12.imprint","IMPRINT",EDGE,{"derivedFrom":subQ3}),-1.0]])]});}
            var Q8;
            {var subQ3=sQuery(id+"F12.wireOp",EDGE,"E91.MirrorCS");Q8=makeQuery(id+"F12.imprint","IMPRINT",FACE,{"disambiguationData":[TD([[makeQuery(id+"F12.imprint","IMPRINT",EDGE,{"derivedFrom":subQ3}),1.0]])]});}
            var Q9;
            {var subQ0=sQuery(id+"F12.wireOp",EDGE,"E117");Q9=makeQuery(id+"F12.imprint","IMPRINT",FACE,{"disambiguationData":[TD([[makeQuery(id+"F12.imprint","IMPRINT",EDGE,{"derivedFrom":subQ0}),-1.0]])]});}
            var Q10;
            {var subQ3=sQuery(id+"F12.wireOp",EDGE,"E71.right");Q10=makeQuery(id+"F12.imprint","IMPRINT",FACE,{"disambiguationData":[TD([[makeQuery(id+"F12.imprint","IMPRINT",EDGE,{"derivedFrom":subQ3}),1.0]])]});}
            var Q11;
            {var subQ0=sQuery(id+"F12.wireOp",EDGE,"E77.right");Q11=makeQuery(id+"F12.imprint","IMPRINT",FACE,{"disambiguationData":[TD([[makeQuery(id+"F12.imprint","IMPRINT",EDGE,{"derivedFrom":subQ0}),1.0]])]});}
            var Q12;
            {var subQ3=sQuery(id+"F12.wireOp",EDGE,"E103");Q12=makeQuery(id+"F12.imprint","IMPRINT",FACE,{"disambiguationData":[TD([[makeQuery(id+"F12.imprint","IMPRINT",EDGE,{"derivedFrom":subQ3}),-1.0]])]});}
            var Q13;
            {var subQ3=sQuery(id+"F12.wireOp",EDGE,"E103");Q13=makeQuery(id+"F12.imprint","IMPRINT",FACE,{"disambiguationData":[TD([[makeQuery(id+"F12.imprint","IMPRINT",EDGE,{"derivedFrom":subQ3}),1.0]])]});}
            var Q14;
            {var subQ3=sQuery(id+"F12.wireOp",EDGE,"E105");Q14=makeQuery(id+"F12.imprint","IMPRINT",FACE,{"disambiguationData":[TD([[makeQuery(id+"F12.imprint","IMPRINT",EDGE,{"derivedFrom":subQ3}),1.0]])]});}
            var Q15;
            {var subQ0=sQuery(id+"F12.wireOp",EDGE,"E105");Q15=makeQuery(id+"F12.imprint","IMPRINT",FACE,{"disambiguationData":[TD([[makeQuery(id+"F12.imprint","IMPRINT",EDGE,{"derivedFrom":subQ0}),-1.0]])]});}
            var Q16;
            {var subQ3=sQuery(id+"F12.wireOp",EDGE,"E106");Q16=makeQuery(id+"F12.imprint","IMPRINT",FACE,{"disambiguationData":[TD([[makeQuery(id+"F12.imprint","IMPRINT",EDGE,{"derivedFrom":subQ3}),1.0]])]});}
            var Q17;
            {var subQ2=sQuery(id+"F12.wireOp",EDGE,"E109.MirrorCS");Q17=makeQuery(id+"F12.imprint","IMPRINT",FACE,{"disambiguationData":[TD([[makeQuery(id+"F12.imprint","IMPRINT",EDGE,{"derivedFrom":subQ2}),-1.0]])]});}
            var Q18;
            {var subQ2=sQuery(id+"F12.wireOp",EDGE,"E109.MirrorCS");Q18=makeQuery(id+"F12.imprint","IMPRINT",FACE,{"disambiguationData":[TD([[makeQuery(id+"F12.imprint","IMPRINT",EDGE,{"derivedFrom":subQ2}),1.0]])]});}
            var Q19;
            {var subQ3=sQuery(id+"F12.wireOp",EDGE,"E110.MirrorCS");Q19=makeQuery(id+"F12.imprint","IMPRINT",FACE,{"disambiguationData":[TD([[makeQuery(id+"F12.imprint","IMPRINT",EDGE,{"derivedFrom":subQ3}),-1.0]])]});}
            var Q20;
            {var subQ2=sQuery(id+"F12.wireOp",EDGE,"E107.MirrorCS");Q20=makeQuery(id+"F12.imprint","IMPRINT",FACE,{"disambiguationData":[TD([[makeQuery(id+"F12.imprint","IMPRINT",EDGE,{"derivedFrom":subQ2}),-1.0]])]});}
            var Q21;
            {var subQ3=sQuery(id+"F12.wireOp",EDGE,"E107.MirrorCS");Q21=makeQuery(id+"F12.imprint","IMPRINT",FACE,{"disambiguationData":[TD([[makeQuery(id+"F12.imprint","IMPRINT",EDGE,{"derivedFrom":subQ3}),1.0]])]});}
            var Q22;
            {var subQ0=sQuery(id+"F12.wireOp",EDGE,"E77.right");Q22=makeQuery(id+"F12.imprint","IMPRINT",FACE,{"disambiguationData":[TD([[makeQuery(id+"F12.imprint","IMPRINT",EDGE,{"derivedFrom":subQ0}),-1.0]])]});}
            var Q23;
            {var subQ0=sQuery(id+"F12.wireOp",EDGE,"E97.MirrorCS");Q23=makeQuery(id+"F12.imprint","IMPRINT",FACE,{"disambiguationData":[TD([[makeQuery(id+"F12.imprint","IMPRINT",EDGE,{"derivedFrom":subQ0}),1.0]])]});}
            var Q24;
            {var subQ5=sQuery(id+"F12.wireOp",EDGE,"E120");Q24=makeQuery(id+"F12.imprint","IMPRINT",FACE,{"disambiguationData":[TD([[makeQuery(id+"F12.imprint","IMPRINT",EDGE,{"derivedFrom":subQ5}),1.0]])]});}
            var Q25;
            {var subQ3=sQuery(id+"F12.wireOp",EDGE,"E124.MirrorCS");Q25=makeQuery(id+"F12.imprint","IMPRINT",FACE,{"disambiguationData":[TD([[makeQuery(id+"F12.imprint","IMPRINT",EDGE,{"derivedFrom":subQ3}),-1.0]])]});}
            var Q26;
            Q26=makeQuery(id+"F62I6zOYyY7Hafo_1.opExtrude","CAP_FACE",FACE,{"disambiguationData":[OSD([sQuery(id+"FRNGrPNkzvzMXeP_1.wireOp",EDGE,"NI18oMSf-gfiH-Vn4B-xRO1-5YiMj2EvDXNp.bottom"),sQuery(id+"FRNGrPNkzvzMXeP_1.wireOp",EDGE,"NI18oMSf-gfiH-Vn4B-xRO1-5YiMj2EvDXNp.top"),sQuery(id+"FRNGrPNkzvzMXeP_1.wireOp",EDGE,"NI18oMSf-gfiH-Vn4B-xRO1-5YiMj2EvDXNp.left"),sQuery(id+"FRNGrPNkzvzMXeP_1.wireOp",EDGE,"NI18oMSf-gfiH-Vn4B-xRO1-5YiMj2EvDXNp.right")])],"isStart":true});
            extrude(context, id + "F13", {"entities" : qUnion([Q0, Q1, Q2, Q3, Q4, Q5, Q6, Q7, Q8, Q9, Q10, Q11, Q12, Q13, Q14, Q15, Q16, Q17, Q18, Q19, Q20, Q21, Q22, Q23, Q24, Q25]), "operationType" : NewBodyOperationType.REMOVE, "depth" : 1221 * mm, "endBoundEntityFace" : qUnion([Q26]), "hasOffset" : true, "offsetDistance" : 240.87 * mm, "hasSecondDirection" : true, "secondDirectionOppositeDirection" : false, "secondDirectionDepth" : 25 * mm});
        }
        {
            var Q0;
            {var subQ5=sQuery(id+"F0.wireOp",EDGE,"E2");Q0=makeQuery(id+"F0.imprint","IMPRINT",FACE,{"disambiguationData":[TD([[makeQuery(id+"F0.imprint","IMPRINT",EDGE,{"derivedFrom":subQ5}),-1.0]])]});}
            var Q1;
            {var subQ5=sQuery(id+"F0.wireOp",EDGE,"E4");var subQ6=sQuery(id+"F0.wireOp",EDGE,"E3");var subQ7=makeQuery(id+"F0.imprint","INTERSECT",VERTEX,{"derivedFrom":[subQ6,subQ5]});Q1=makeQuery(id+"F0.imprint","IMPRINT",FACE,{"disambiguationData":[TD([[makeQuery(id+"F0.imprint","IMPRINT",EDGE,{"disambiguationData":[TD([[subQ7,1.0]])],"derivedFrom":subQ6}),-1.0]])]});}
            var Q2;
            {var subQ0=sQuery(id+"F0.wireOp",EDGE,"E28");Q2=makeQuery(id+"F0.imprint","IMPRINT",FACE,{"disambiguationData":[TD([[makeQuery(id+"F0.imprint","IMPRINT",EDGE,{"derivedFrom":subQ0}),-1.0]])]});}
            var Q3;
            {var subQ5=sQuery(id+"F0.wireOp",EDGE,"E31");Q3=makeQuery(id+"F0.imprint","IMPRINT",FACE,{"disambiguationData":[TD([[makeQuery(id+"F0.imprint","IMPRINT",EDGE,{"derivedFrom":subQ5}),1.0]])]});}
            var Q4;
            {var subQ5=sQuery(id+"F0.wireOp",EDGE,"E33");Q4=makeQuery(id+"F0.imprint","IMPRINT",FACE,{"disambiguationData":[TD([[makeQuery(id+"F0.imprint","IMPRINT",EDGE,{"derivedFrom":subQ5}),1.0]])]});}
            extrude(context, id + "F14", {"entities" : qUnion([Q0, Q1, Q2, Q3, Q4]), "operationType" : NewBodyOperationType.ADD, "depth" : 200 * mm, "offsetDistance" : 25 * mm});
        }
        {
            var Q0;
            Q0=qSketchRegion(id+"F7",true);
            extrude(context, id + "F15", {"entities" : qUnion([Q0]), "operationType" : NewBodyOperationType.REMOVE, "depth" : 500 * mm, "offsetDistance" : 25 * mm, "symmetric" : true});
        }
        {
            var Q0;
            Q0=makeQuery(id+"F1.opExtrude","CAP_EDGE",EDGE,{"disambiguationData":[OSD([sQuery(id+"F0.wireOp",EDGE,"E3")])],"isStart":true});
            var Q1;
            Q1=makeQuery(id+"F1.opExtrude","CAP_EDGE",EDGE,{"disambiguationData":[OSD([sQuery(id+"F0.wireOp",EDGE,"E3")])],"isStart":false});
            var Q2;
            Q2=makeQuery(id+"F1.opExtrude","CAP_EDGE",EDGE,{"disambiguationData":[OSD([sQuery(id+"F0.wireOp",EDGE,"ae0f4dbe-3dcb-452f-a479-656d4edaf589")])],"isStart":true});
            var Q3;
            Q3=makeQuery(id+"F8.boolean.opBoolean","MERGE",EDGE,{"derivedFrom":[makeQuery(id+"F1.opExtrude","CAP_EDGE",EDGE,{"disambiguationData":[OSD([sQuery(id+"F0.wireOp",EDGE,"E0"),sQuery(id+"F0.wireOp",EDGE,"E5")])],"isStart":true}),makeQuery(id+"F8.opExtrude","SWEPT_EDGE",EDGE,{"disambiguationData":[OSD([sQuery(id+"F4.wireOp",EDGE,"E38"),sQuery(id+"F4.wireOp",EDGE,"E51.0")])]})]});
            var Q4;
            Q4=makeQuery(id+"F8.boolean.opBoolean","MERGE",EDGE,{"derivedFrom":[makeQuery(id+"F1.opExtrude","CAP_EDGE",EDGE,{"disambiguationData":[OSD([sQuery(id+"F0.wireOp",EDGE,"E0"),sQuery(id+"F0.wireOp",EDGE,"E5")])],"isStart":false}),makeQuery(id+"F8.opExtrude","SWEPT_EDGE",EDGE,{"disambiguationData":[OSD([sQuery(id+"F4.wireOp",EDGE,"E39"),sQuery(id+"F4.wireOp",EDGE,"E51.0")])]})]});
            fillet(context, id + "F16", {"entities" : qUnion([Q0, Q1, Q2, Q3, Q4]), "radius" : 15 * mm, "tangentPropagation" : true, "allowEdgeOverflow" : false});
        }
        {
            var Q0;
            Q0=qCreatedBy(id+"F11.planeOp",FACE);
            var sketch = newSketch(context, id + "F17", { "sketchPlane" : qUnion([Q0])});
            skLineSegment(sketch, "E129.bottom", {"start": v(0, 0) * mm, "end": v(-200, 0) * mm});
            skLineSegment(sketch, "E130", {"start": v(-94.5, 76) * mm, "end": v(0, 76) * mm});
            skLineSegment(sketch, "E131.bottom", {"start": v(-94.5, 76) * mm, "end": v(-105.5, 76) * mm});
            skLineSegment(sketch, "E131.top", {"start": v(-94.5, 87) * mm, "end": v(-105.5, 87) * mm});
            skLineSegment(sketch, "E131.left", {"start": v(-94.5, 76) * mm, "end": v(-94.5, 87) * mm});
            skLineSegment(sketch, "E131.right", {"start": v(-105.5, 76) * mm, "end": v(-105.5, 87) * mm});
            skLineSegment(sketch, "E132", {"start": v(-94.5, 76) * mm, "end": v(-94.5, 0) * mm});
            skSolve(sketch);
        }
        {
            var Q0;
            Q0 = qSketchRegion(id + "F17", true);
            var Q1;
            Q1=makeQuery(id+"F62I6zOYyY7Hafo_1.opExtrude","CAP_FACE",FACE,{"disambiguationData":[OSD([sQuery(id+"FRNGrPNkzvzMXeP_1.wireOp",EDGE,"NI18oMSf-gfiH-Vn4B-xRO1-5YiMj2EvDXNp.bottom"),sQuery(id+"FRNGrPNkzvzMXeP_1.wireOp",EDGE,"NI18oMSf-gfiH-Vn4B-xRO1-5YiMj2EvDXNp.top"),sQuery(id+"FRNGrPNkzvzMXeP_1.wireOp",EDGE,"NI18oMSf-gfiH-Vn4B-xRO1-5YiMj2EvDXNp.left"),sQuery(id+"FRNGrPNkzvzMXeP_1.wireOp",EDGE,"NI18oMSf-gfiH-Vn4B-xRO1-5YiMj2EvDXNp.right")])],"isStart":true});
            extrude(context, id + "F18", {"entities" : qUnion([Q0]), "operationType" : NewBodyOperationType.REMOVE, "depth" : 1250 * mm, "endBoundEntityFace" : qUnion([Q1]), "hasOffset" : true, "offsetDistance" : 140.87 * mm, "hasSecondDirection" : true, "secondDirectionOppositeDirection" : false, "secondDirectionDepth" : 1150 * mm});
        }
        {
            var Q0;
            Q0=qCreatedBy(makeId("Top.planeOp"),FACE);
            var sketch = newSketch(context, id + "F19", { "sketchPlane" : qUnion([Q0])});
            skLineSegment(sketch, "E133", {"start": v(0, 0) * mm, "end": v(0, -100) * mm});
            skLineSegment(sketch, "E134", {"start": v(0, -100) * mm, "end": v(223, -100) * mm});
            skLineSegment(sketch, "E135.bottom", {"start": v(228.5, -105.5) * mm, "end": v(217.5, -105.5) * mm});
            skLineSegment(sketch, "E135.top", {"start": v(228.5, -94.5) * mm, "end": v(217.5, -94.5) * mm});
            skLineSegment(sketch, "E135.left", {"start": v(228.5, -105.5) * mm, "end": v(228.5, -94.5) * mm});
            skLineSegment(sketch, "E135.right", {"start": v(217.5, -105.5) * mm, "end": v(217.5, -94.5) * mm});
            skPoint(sketch, "E135.middle", {"position": v(223, -100) * mm});
            skSolve(sketch);
        }
        {
            var Q0;
            Q0 = qSketchRegion(id + "F19", true);
            extrude(context, id + "F20", {"entities" : qUnion([Q0]), "operationType" : NewBodyOperationType.REMOVE, "depth" : 138 * mm, "offsetDistance" : 25 * mm, "hasSecondDirection" : true, "secondDirectionOppositeDirection" : false, "secondDirectionDepth" : 76 * mm});
        }
        {
            var Q0;
            Q0=makeQuery(id+"F0.imprint","IMPRINT",FACE,{"disambiguationData":[TD([[makeQuery(id+"F0.imprint","IMPRINT",EDGE,{"derivedFrom":sQuery(id+"F0.wireOp",EDGE,"E16.bottom")}),1.0]])]});
            var Q1;
            Q1=makeQuery(id+"F0.imprint","IMPRINT",FACE,{"disambiguationData":[TD([[makeQuery(id+"F0.imprint","IMPRINT",EDGE,{"derivedFrom":sQuery(id+"F0.wireOp",EDGE,"E17.bottom")}),1.0]])]});
            var Q2;
            Q2=makeQuery(id+"F0.imprint","IMPRINT",FACE,{"disambiguationData":[TD([[makeQuery(id+"F0.imprint","IMPRINT",EDGE,{"derivedFrom":sQuery(id+"F0.wireOp",EDGE,"E15")}),1.0]])]});
            extrude(context, id + "F21", {"entities" : qUnion([Q0, Q1, Q2]), "operationType" : NewBodyOperationType.REMOVE, "endBound" : BoundingType.THROUGH_ALL, "depth" : 25 * mm, "offsetDistance" : 25 * mm});
        }
    });
